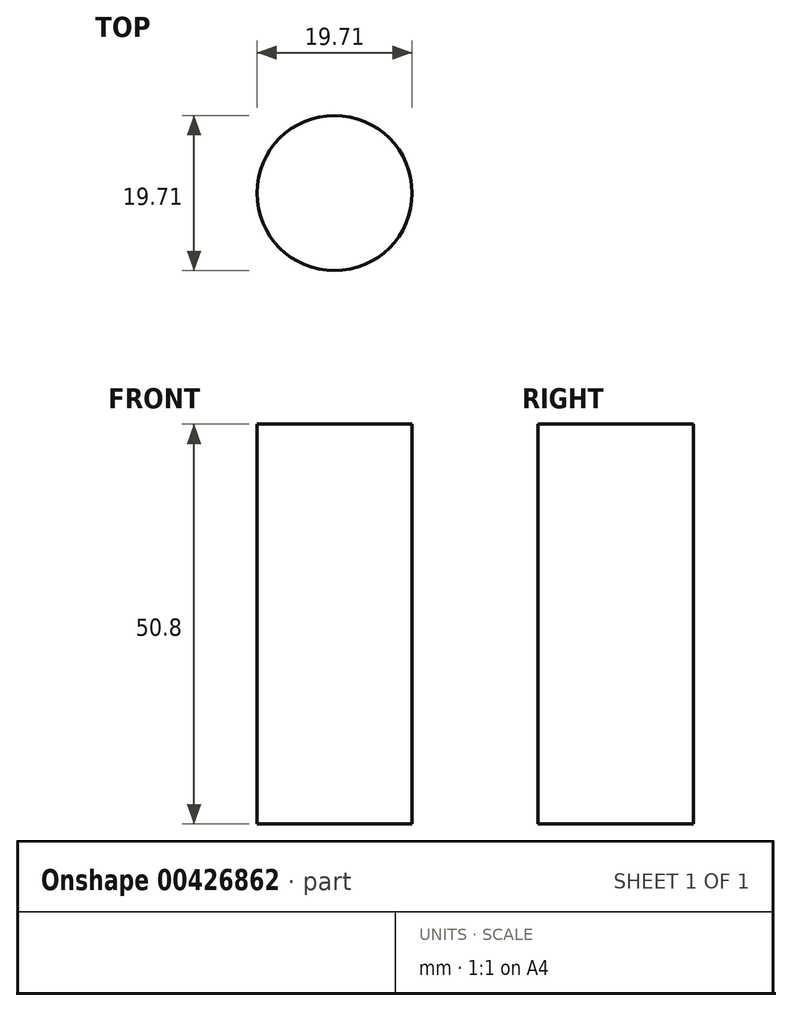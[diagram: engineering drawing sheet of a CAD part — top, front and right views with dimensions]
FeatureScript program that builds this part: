
annotation { "Feature Type Name" : "Feature", "Feature Type Description" : "" }
export const myFeature = defineFeature(function(context is Context, id is Id, definition is map)
    precondition{}
    {
        {
            var Q0;
            Q0=qCreatedBy(makeId("Top.planeOp"),FACE);
            var sketch = newSketch(context, id + "F0", { "sketchPlane" : qUnion([Q0])});
            skCircle(sketch, "E0", {"center": v(-0.76, 0.68) * mm, "radius": 9.86 * mm});
            skSolve(sketch);
        }
        {
            var Q0;
            Q0 = qConstructionFilter(qBodyType(qCreatedBy(id + "F0" ,EDGE), BodyType.WIRE), ConstructionObject.NO);
            extrude(context, id + "F1", {"bodyType" : ToolBodyType.SURFACE, "surfaceEntities" : qUnion([Q0]), "depth" : 50.8 * mm});
        }
    });
